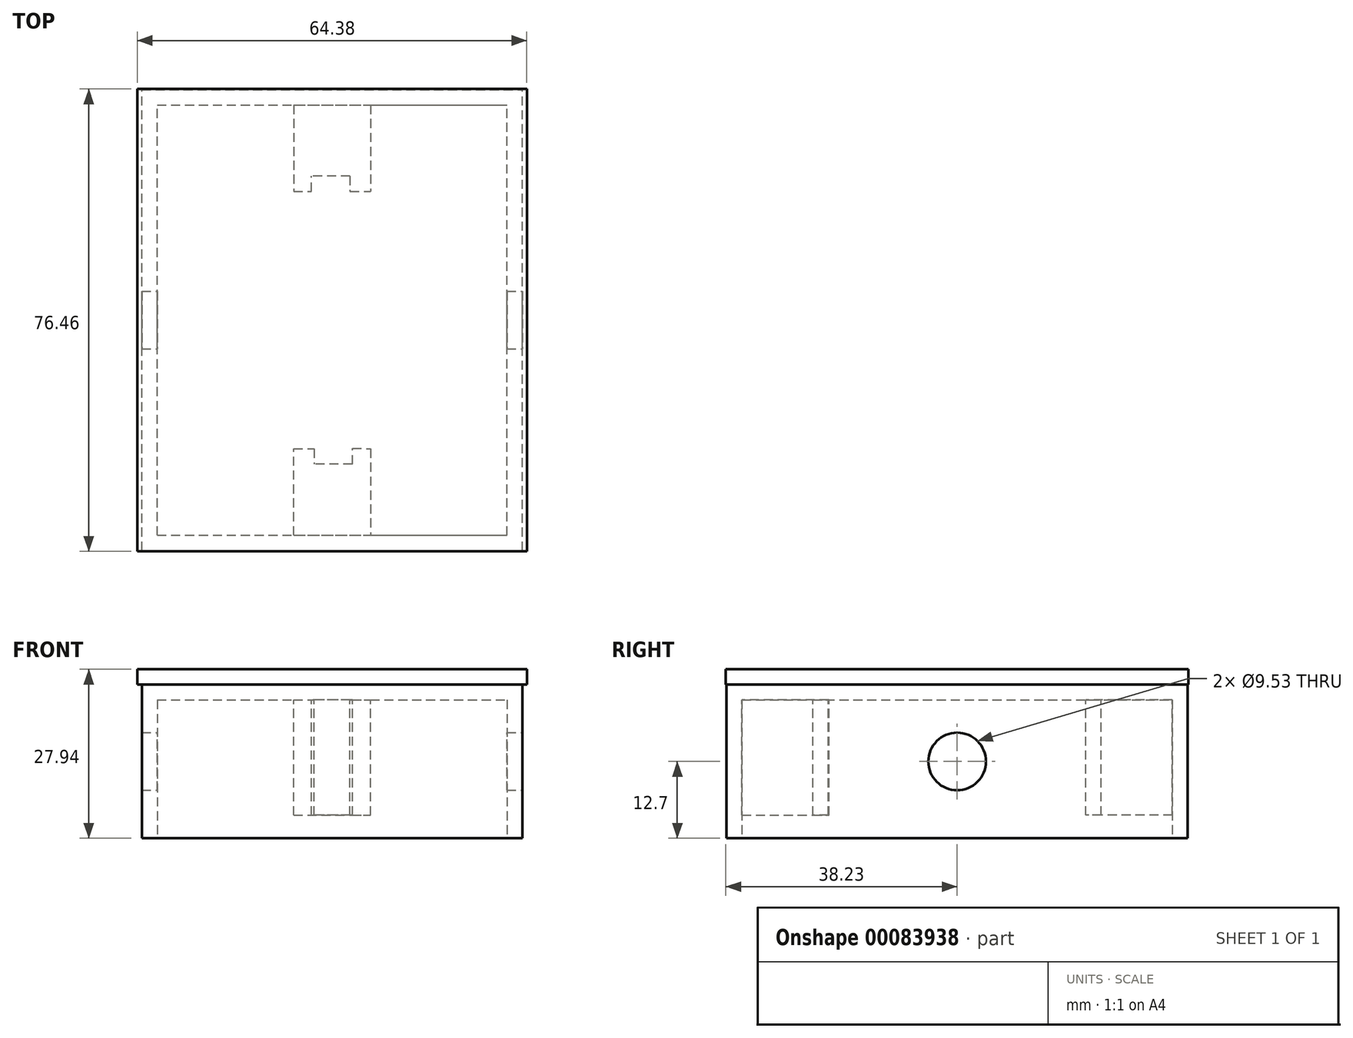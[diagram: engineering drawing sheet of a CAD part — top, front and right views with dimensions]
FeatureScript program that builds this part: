
annotation { "Feature Type Name" : "Feature", "Feature Type Description" : "" }
export const myFeature = defineFeature(function(context is Context, id is Id, definition is map)
    precondition{}
    {
        {
            var Q0;
            Q0=qCreatedBy(makeId("Front.planeOp"),FACE);
            var sketch = newSketch(context, id + "F0", { "sketchPlane" : qUnion([Q0])});
            skLineSegment(sketch, "E0.bottom", {"start": v(-31.43, 12.7) * mm, "end": v(31.43, 12.7) * mm});
            skLineSegment(sketch, "E0.top", {"start": v(-31.43, -12.7) * mm, "end": v(31.43, -12.7) * mm});
            skLineSegment(sketch, "E0.left", {"start": v(-31.43, 12.7) * mm, "end": v(-31.43, -12.7) * mm});
            skLineSegment(sketch, "E0.right", {"start": v(31.43, 12.7) * mm, "end": v(31.43, -12.7) * mm});
            skPoint(sketch, "E0.middle", {"position": v(0, 0) * mm});
            skSolve(sketch);
        }
        {
            var Q0;
            Q0=makeQuery(id+"F0.imprint","IMPRINT",FACE,{"disambiguationData":[TD([[makeQuery(id+"F0.imprint","IMPRINT",EDGE,{"derivedFrom":sQuery(id+"F0.wireOp",EDGE,"E0.bottom")}),-1.0]])]});
            extrude(context, id + "F1", {"entities" : qUnion([Q0]), "depth" : 76.2 * mm});
        }
        {
            var Q0;
            Q0=makeQuery(id+"F1.opExtrude","SWEPT_FACE",FACE,{"disambiguationData":[OSD([sQuery(id+"F0.wireOp",EDGE,"E0.right")])]});
            var sketch = newSketch(context, id + "F2", { "sketchPlane" : qUnion([Q0])});
            skPoint(sketch, "E1.endSnap0", {"position": v(-38.1, 12.7) * mm});
            skCircle(sketch, "E2", {"center": v(-38.1, 0) * mm, "radius": 4.76 * mm});
            skSolve(sketch);
        }
        {
            var Q0;
            Q0=makeQuery(id+"F1.opExtrude","SWEPT_FACE",FACE,{"disambiguationData":[OSD([sQuery(id+"F0.wireOp",EDGE,"E0.top")])]});
            shell(context, id + "F3", {"entities" : qUnion([Q0]), "thickness" : 2.54 * mm});
        }
        {
            var Q0;
            Q0=makeQuery(id+"F1.opExtrude","SWEPT_FACE",FACE,{"disambiguationData":[OSD([sQuery(id+"F0.wireOp",EDGE,"E0.bottom")])]});
            var sketch = newSketch(context, id + "F4", { "sketchPlane" : qUnion([Q0])});
            skLineSegment(sketch, "E3.bottom", {"start": v(32.2, 0.13) * mm, "end": v(-32.2, 0.13) * mm});
            skLineSegment(sketch, "E3.top", {"start": v(32.2, -76.33) * mm, "end": v(-32.2, -76.33) * mm});
            skLineSegment(sketch, "E3.left", {"start": v(32.2, 0.13) * mm, "end": v(32.2, -76.33) * mm});
            skLineSegment(sketch, "E3.right", {"start": v(-32.2, 0.13) * mm, "end": v(-32.2, -76.33) * mm});
            skPoint(sketch, "E3.middle", {"position": v(0, -38.1) * mm});
            skPoint(sketch, "E3.middle.positionSnap0", {"position": v(-31.43, -38.1) * mm});
            skPoint(sketch, "E3.centerSnap0", {"position": v(-31.43, -38.1) * mm});
            skSolve(sketch);
        }
        {
            var Q0;
            Q0 = qSketchRegion(id + "F4", true);
            extrude(context, id + "F5", {"entities" : qUnion([Q0]), "operationType" : NewBodyOperationType.ADD, "depth" : 2.54 * mm});
        }
        {
            var Q0;
            Q0=makeQuery(id+"F2.imprint","IMPRINT",FACE,{"disambiguationData":[TD([[makeQuery(id+"F2.imprint","IMPRINT",EDGE,{"derivedFrom":sQuery(id+"F2.wireOp",EDGE,"E2")}),1.0]])]});
            var Q1;
            Q1=sQuery(id+"F2.wireOp",EDGE,"E2");
            extrude(context, id + "F6", {"entities" : qUnion([Q0]), "operationType" : NewBodyOperationType.REMOVE, "surfaceEntities" : qUnion([Q1]), "endBound" : BoundingType.THROUGH_ALL, "oppositeDirection" : true, "depth" : 25.4 * mm});
        }
        {
            var Q0;
            Q0=makeQuery(id+"F3.opShell","OFFSET_FACE",FACE,{"disambiguationData":[OSD([sQuery(id+"F0.wireOp",EDGE,"E0.bottom")])]});
            var sketch = newSketch(context, id + "F7", { "sketchPlane" : qUnion([Q0])});
            skLineSegment(sketch, "E4.bottom", {"start": v(3.37, 61.91) * mm, "end": v(-2.98, 61.91) * mm});
            skLineSegment(sketch, "E4.top", {"start": v(2.98, 14.29) * mm, "end": v(-3.37, 14.29) * mm});
            skPoint(sketch, "E4.middle", {"position": v(0, 38.1) * mm});
            skPoint(sketch, "E4.middle.positionSnap0", {"position": v(-28.9, 38.1) * mm});
            skPoint(sketch, "E4.centerSnap0", {"position": v(-28.9, 38.1) * mm});
            skLineSegment(sketch, "E5", {"start": v(0, 73.66) * mm, "end": v(-6.35, 73.66) * mm});
            skLineSegment(sketch, "E6", {"start": v(-6.35, 73.66) * mm, "end": v(-6.35, 61.91) * mm});
            skLineSegment(sketch, "E7", {"start": v(0, 73.66) * mm, "end": v(6.35, 73.66) * mm});
            skLineSegment(sketch, "E8", {"start": v(6.35, 73.66) * mm, "end": v(6.35, 61.91) * mm});
            skLineSegment(sketch, "E9", {"start": v(-6.35, 61.91) * mm, "end": v(-6.35, 59.37) * mm});
            skLineSegment(sketch, "E10", {"start": v(6.35, 59.37) * mm, "end": v(6.35, 61.91) * mm});
            skLineSegment(sketch, "E11", {"start": v(-6.35, 59.37) * mm, "end": v(-2.98, 59.37) * mm});
            skLineSegment(sketch, "E12", {"start": v(-2.98, 59.37) * mm, "end": v(-2.98, 61.91) * mm});
            skLineSegment(sketch, "E13", {"start": v(3.37, 61.91) * mm, "end": v(3.37, 59.28) * mm});
            skLineSegment(sketch, "E14", {"start": v(3.37, 59.28) * mm, "end": v(6.35, 59.37) * mm});
            skLineSegment(sketch, "E15", {"start": v(-6.35, 2.54) * mm, "end": v(6.35, 2.54) * mm});
            skLineSegment(sketch, "E16", {"start": v(6.35, 2.54) * mm, "end": v(6.35, 14.29) * mm});
            skLineSegment(sketch, "E17", {"start": v(-6.35, 2.54) * mm, "end": v(-6.35, 14.29) * mm});
            skLineSegment(sketch, "E18", {"start": v(-6.35, 14.29) * mm, "end": v(-6.35, 16.83) * mm});
            skLineSegment(sketch, "E19", {"start": v(-6.35, 16.83) * mm, "end": v(-3.37, 16.83) * mm});
            skLineSegment(sketch, "E20", {"start": v(-3.37, 16.83) * mm, "end": v(-3.37, 14.29) * mm});
            skLineSegment(sketch, "E21", {"start": v(2.98, 14.29) * mm, "end": v(2.98, 16.83) * mm});
            skLineSegment(sketch, "E22", {"start": v(2.98, 16.83) * mm, "end": v(6.35, 16.83) * mm});
            skLineSegment(sketch, "E23", {"start": v(6.35, 16.83) * mm, "end": v(6.35, 14.29) * mm});
            skSolve(sketch);
        }
        {
            var Q0;
            Q0 = qSketchRegion(id + "F7", true);
            extrude(context, id + "F8", {"entities" : qUnion([Q0]), "operationType" : NewBodyOperationType.ADD, "depth" : 19.05 * mm});
        }
    });
